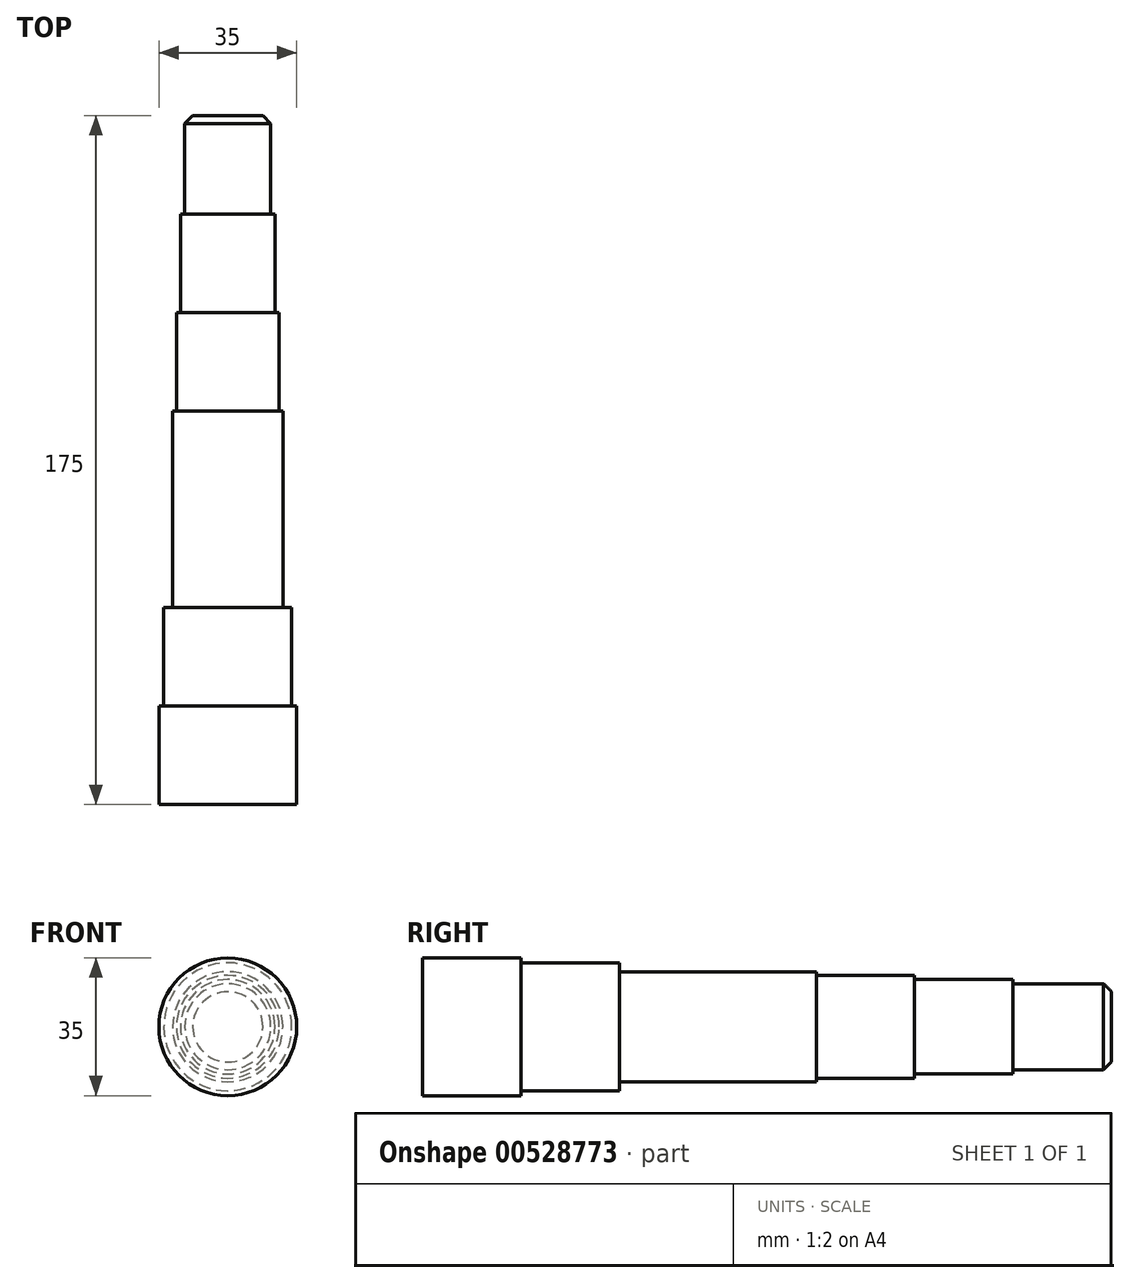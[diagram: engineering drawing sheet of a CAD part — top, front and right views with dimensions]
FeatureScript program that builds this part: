
annotation { "Feature Type Name" : "Feature", "Feature Type Description" : "" }
export const myFeature = defineFeature(function(context is Context, id is Id, definition is map)
    precondition{}
    {
        {
            var Q0;
            Q0=qCreatedBy(makeId("Front.planeOp"),FACE);
            var sketch = newSketch(context, id + "F0", { "sketchPlane" : qUnion([Q0])});
            skCircle(sketch, "E0", {"center": v(0, 0) * mm, "radius": 17.5 * mm});
            skSolve(sketch);
        }
        {
            var Q0;
            Q0=makeQuery(id+"F0.imprint","IMPRINT",FACE,{"disambiguationData":[TD([[makeQuery(id+"F0.imprint","IMPRINT",EDGE,{"derivedFrom":sQuery(id+"F0.wireOp",EDGE,"E0")}),1.0]])]});
            extrude(context, id + "F1", {"entities" : qUnion([Q0]), "depth" : 25 * mm, "offsetDistance" : 25 * mm});
        }
        {
            var Q0;
            Q0=makeQuery(id+"F1.opExtrude","CAP_FACE",FACE,{"disambiguationData":[OSD([sQuery(id+"F0.wireOp",EDGE,"E0")])],"isStart":true});
            var sketch = newSketch(context, id + "F2", { "sketchPlane" : qUnion([Q0])});
            skCircle(sketch, "E1", {"center": v(0, 0) * mm, "radius": 16.25 * mm});
            skSolve(sketch);
        }
        {
            var Q0;
            Q0 = qSketchRegion(id + "F2", true);
            extrude(context, id + "F3", {"entities" : qUnion([Q0]), "operationType" : NewBodyOperationType.ADD, "depth" : 25 * mm, "offsetDistance" : 25 * mm});
        }
        {
            var Q0;
            Q0=makeQuery(id+"F3.opExtrude","CAP_FACE",FACE,{"disambiguationData":[OSD([sQuery(id+"F2.wireOp",EDGE,"E1")])],"isStart":false});
            var sketch = newSketch(context, id + "F4", { "sketchPlane" : qUnion([Q0])});
            skCircle(sketch, "E2", {"center": v(0, 0) * mm, "radius": 14 * mm});
            skSolve(sketch);
        }
        {
            var Q0;
            Q0 = qSketchRegion(id + "F4", true);
            extrude(context, id + "F5", {"entities" : qUnion([Q0]), "operationType" : NewBodyOperationType.ADD, "depth" : 50 * mm, "offsetDistance" : 25 * mm});
        }
        {
            var Q0;
            Q0=makeQuery(id+"F5.opExtrude","CAP_FACE",FACE,{"disambiguationData":[OSD([sQuery(id+"F4.wireOp",EDGE,"E2")])],"isStart":false});
            var sketch = newSketch(context, id + "F6", { "sketchPlane" : qUnion([Q0])});
            skCircle(sketch, "E3", {"center": v(0, 0) * mm, "radius": 13.05 * mm});
            skSolve(sketch);
        }
        {
            var Q0;
            Q0 = qSketchRegion(id + "F6", true);
            extrude(context, id + "F7", {"entities" : qUnion([Q0]), "operationType" : NewBodyOperationType.ADD, "depth" : 25 * mm, "offsetDistance" : 25 * mm});
        }
        {
            var Q0;
            Q0=makeQuery(id+"F7.opExtrude","CAP_FACE",FACE,{"disambiguationData":[OSD([sQuery(id+"F6.wireOp",EDGE,"E3")])],"isStart":false});
            var sketch = newSketch(context, id + "F8", { "sketchPlane" : qUnion([Q0])});
            skCircle(sketch, "E4", {"center": v(0, 0) * mm, "radius": 12 * mm});
            skSolve(sketch);
        }
        {
            var Q0;
            Q0 = qSketchRegion(id + "F8", true);
            extrude(context, id + "F9", {"entities" : qUnion([Q0]), "operationType" : NewBodyOperationType.ADD, "depth" : 25 * mm, "offsetDistance" : 25 * mm});
        }
        {
            var Q0;
            Q0=makeQuery(id+"F9.opExtrude","CAP_FACE",FACE,{"disambiguationData":[OSD([sQuery(id+"F8.wireOp",EDGE,"E4")])],"isStart":false});
            var sketch = newSketch(context, id + "F10", { "sketchPlane" : qUnion([Q0])});
            skCircle(sketch, "E5", {"center": v(0, 0) * mm, "radius": 10.93 * mm});
            skSolve(sketch);
        }
        {
            var Q0;
            Q0 = qSketchRegion(id + "F10", true);
            extrude(context, id + "F11", {"entities" : qUnion([Q0]), "operationType" : NewBodyOperationType.ADD, "depth" : 25 * mm, "offsetDistance" : 25 * mm});
        }
        {
            var Q0;
            Q0=makeQuery(id+"F11.opExtrude","CAP_FACE",FACE,{"disambiguationData":[OSD([sQuery(id+"F10.wireOp",EDGE,"E5")])],"isStart":false});
            chamfer(context, id + "F12", {"entities" : qUnion([Q0]), "width" : 2 * mm, "tangentPropagation" : true});
        }
    });
